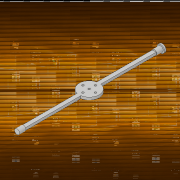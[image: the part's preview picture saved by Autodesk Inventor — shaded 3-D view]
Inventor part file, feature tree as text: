
AUTODESK INVENTOR PART (.ipt)
format: ipt  version: 2017 (Build 210142000, 142)  size: 179,200 bytes
history: native  units: in
note: dims shown in document units (in); Inventor stores cm internally (conversion verified against a paired STEP export)
features: sketch x6, extrude x5, hole x1
ambient origin geometry x8: Origin, YZ Plane, XZ Plane, XY Plane, X Axis, Y Axis, Z Axis, Center Point
bodies: Solid1 (feature_tree)
feature tree (12):
  extrude  "Extrusion1"  Depth=0.2in
  extrude  "Extrusion2"  Depth=10.229in
  extrude  "Extrusion3"  Depth=0.1499in
  extrude  "Extrusion4"  Depth=0.5in
  extrude  "Extrusion5"  Depth=0.5in
  hole  "Hole1"  [1 undecoded]
  sketch  "Sketch1"  dims[d0=0.3in d1=0.2in]
  sketch  "Sketch2"  dims[d2=10.229in d3=0.0in d4=0.4in]
  sketch  "Sketch3"  dims[d5=0.1in d6=0.1499in]
  sketch  "Sketch4"  dims[d7=0.5in d8=0.0in d9=0.4in]
  sketch  "Sketch5"  dims[d10=0.5in d11=0.0in d12=0.6in]
  sketch  "Sketch6"  dims[d13=0.125in d14=0.0in d15=0.125in d16=10.229in d17=5.1145in d18=1.5748in d19=1.0in d20=0.0in d21=1.5748in d22=0.0in d23=0.0in d24=0.9843in d25=0.1575in d26=0.75in d27=0.375in d28=0.25in d29=0.5635in d30=1.0in d31=0.8108in]
note: 1 required parameter value undecoded (feature->parameter linkage not recoverable at this tier; creation-order binding heuristic only, values carry confidence <= 0.55)
